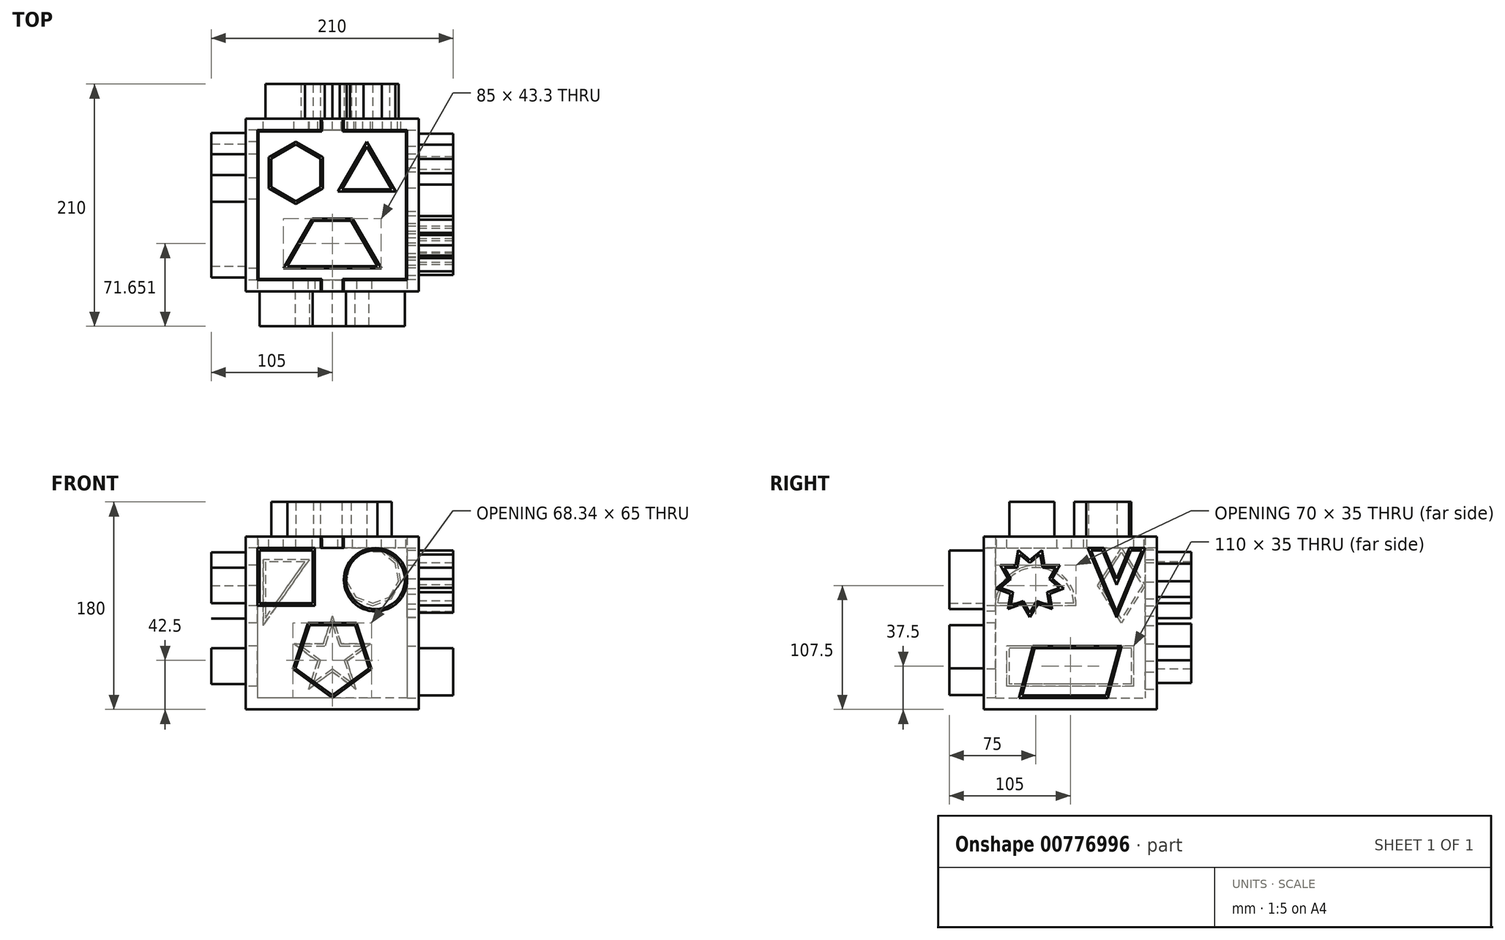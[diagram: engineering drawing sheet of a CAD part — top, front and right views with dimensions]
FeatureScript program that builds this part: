
annotation { "Feature Type Name" : "Feature", "Feature Type Description" : "" }
export const myFeature = defineFeature(function(context is Context, id is Id, definition is map)
    precondition{}
    {
        {
            var Q0;
            Q0=qCreatedBy(makeId("Top.planeOp"),FACE);
            var sketch = newSketch(context, id + "F0", { "sketchPlane" : qUnion([Q0])});
            skLineSegment(sketch, "E0.bottom", {"start": v(0, 0) * mm, "end": v(-150, 0) * mm});
            skLineSegment(sketch, "E0.top", {"start": v(0, 150) * mm, "end": v(-150, 150) * mm});
            skLineSegment(sketch, "E0.left", {"start": v(0, 0) * mm, "end": v(0, 150) * mm});
            skLineSegment(sketch, "E0.right", {"start": v(-150, 0) * mm, "end": v(-150, 150) * mm});
            skSolve(sketch);
        }
        {
            var Q0;
            Q0=makeQuery(id+"F0.imprint","IMPRINT",FACE,{"disambiguationData":[TD([[makeQuery(id+"F0.imprint","IMPRINT",EDGE,{"derivedFrom":sQuery(id+"F0.wireOp",EDGE,"E0.bottom")}),-1.0]])]});
            extrude(context, id + "F1", {"entities" : qUnion([Q0]), "depth" : 150 * mm, "offsetDistance" : 25 * mm});
        }
        {
            var Q0;
            Q0=makeQuery(id+"F1.opExtrude","CAP_FACE",FACE,{"disambiguationData":[OSD([sQuery(id+"F0.wireOp",EDGE,"E0.bottom"),sQuery(id+"F0.wireOp",EDGE,"E0.top"),sQuery(id+"F0.wireOp",EDGE,"E0.left"),sQuery(id+"F0.wireOp",EDGE,"E0.right")])],"isStart":false});
            shell(context, id + "F2", {"entities" : qUnion([Q0]), "thickness" : 10 * mm});
        }
        {
            var Q0;
            Q0=makeQuery(id+"F1.opExtrude","CAP_FACE",FACE,{"disambiguationData":[OSD([sQuery(id+"F0.wireOp",EDGE,"E0.bottom"),sQuery(id+"F0.wireOp",EDGE,"E0.top"),sQuery(id+"F0.wireOp",EDGE,"E0.left"),sQuery(id+"F0.wireOp",EDGE,"E0.right")])],"isStart":false});
            var sketch = newSketch(context, id + "F3", { "sketchPlane" : qUnion([Q0])});
            skLineSegment(sketch, "E1.bottom", {"start": v(-10, 10) * mm, "end": v(-65, 10) * mm});
            skLineSegment(sketch, "E1.top", {"start": v(-10, 140) * mm, "end": v(-65, 140) * mm});
            skLineSegment(sketch, "E1.left", {"start": v(-10, 10) * mm, "end": v(-10, 140) * mm});
            skLineSegment(sketch, "E1.right", {"start": v(-140, 10) * mm, "end": v(-140, 140) * mm});
            skPoint(sketch, "E2", {"position": v(-75, 140) * mm});
            skLineSegment(sketch, "E3", {"start": v(-75, 140) * mm, "end": v(-85, 140) * mm});
            skLineSegment(sketch, "E4", {"start": v(-85, 140) * mm, "end": v(-85, 150) * mm});
            skLineSegment(sketch, "E5", {"start": v(-85, 150) * mm, "end": v(-65, 150) * mm});
            skLineSegment(sketch, "E6", {"start": v(-65, 150) * mm, "end": v(-65, 140) * mm});
            skLineSegment(sketch, "E7", {"start": v(-65, 140) * mm, "end": v(-75, 140) * mm});
            skLineSegment(sketch, "E8", {"start": v(-140, 75) * mm, "end": v(-10, 75) * mm, "construction": true});
            skLineSegment(sketch, "E9.MirrorCS", {"start": v(-75, 10) * mm, "end": v(-85, 10) * mm});
            skLineSegment(sketch, "E10.MirrorCS", {"start": v(-65, 10) * mm, "end": v(-75, 10) * mm});
            skLineSegment(sketch, "E11.MirrorCS", {"start": v(-85, 0) * mm, "end": v(-65, 0) * mm});
            skLineSegment(sketch, "E12.MirrorCS", {"start": v(-85, 10) * mm, "end": v(-85, 0) * mm});
            skLineSegment(sketch, "E13.MirrorCS", {"start": v(-65, 0) * mm, "end": v(-65, 10) * mm});
            skLineSegment(sketch, "E14", {"start": v(-85, 140) * mm, "end": v(-140, 140) * mm});
            skLineSegment(sketch, "E15", {"start": v(-65, 140) * mm, "end": v(-85, 140) * mm});
            skLineSegment(sketch, "E16", {"start": v(-85, 10) * mm, "end": v(-140, 10) * mm});
            skLineSegment(sketch, "E17", {"start": v(-65, 10) * mm, "end": v(-85, 10) * mm});
            skLineSegment(sketch, "E18.0", {"start": v(-84, 139) * mm, "end": v(-84, 150) * mm});
            skLineSegment(sketch, "E18.1", {"start": v(-84, 11) * mm, "end": v(-84, 0) * mm});
            skLineSegment(sketch, "E18.2", {"start": v(-84, 11) * mm, "end": v(-139, 11) * mm});
            skLineSegment(sketch, "E18.3", {"start": v(-139, 11) * mm, "end": v(-139, 139) * mm});
            skLineSegment(sketch, "E18.4", {"start": v(-84, 139) * mm, "end": v(-139, 139) * mm});
            skLineSegment(sketch, "E19.0", {"start": v(5, -5) * mm, "end": v(5, 155) * mm});
            skLineSegment(sketch, "E19.1", {"start": v(-155, -5) * mm, "end": v(5, -5) * mm});
            skLineSegment(sketch, "E19.2", {"start": v(-155, 155) * mm, "end": v(-155, -5) * mm});
            skLineSegment(sketch, "E19.3", {"start": v(5, 155) * mm, "end": v(-155, 155) * mm});
            skLineSegment(sketch, "E20.0", {"start": v(-66, 0) * mm, "end": v(-66, 11) * mm});
            skLineSegment(sketch, "E20.1", {"start": v(-66, 150) * mm, "end": v(-66, 139) * mm});
            skLineSegment(sketch, "E20.2", {"start": v(-11, 139) * mm, "end": v(-66, 139) * mm});
            skLineSegment(sketch, "E20.3", {"start": v(-11, 11) * mm, "end": v(-11, 139) * mm});
            skLineSegment(sketch, "E20.4", {"start": v(-11, 11) * mm, "end": v(-66, 11) * mm});
            skSolve(sketch);
        }
        {
            var Q0;
            {var subQ3=sQuery(id+"F3.wireOp",EDGE,"E1.left");Q0=makeQuery(id+"F3.imprint","IMPRINT",FACE,{"disambiguationData":[TD([[makeQuery(id+"F3.imprint","IMPRINT",EDGE,{"derivedFrom":subQ3}),1.0]])]});}
            var sketch = newSketch(context, id + "F4", { "sketchPlane" : qUnion([Q0])});
            skCircle(sketch, "E21.cCircle", {"center": v(-106.62, 103) * mm, "radius": 23.38 * mm, "construction": true});
            skLineSegment(sketch, "E21.0", {"start": v(-106.62, 130) * mm, "end": v(-83.23, 116.5) * mm});
            skLineSegment(sketch, "E21.1", {"start": v(-83.23, 116.5) * mm, "end": v(-83.23, 89.5) * mm});
            skLineSegment(sketch, "E21.2", {"start": v(-83.23, 89.5) * mm, "end": v(-106.62, 76) * mm});
            skLineSegment(sketch, "E21.3", {"start": v(-106.62, 76) * mm, "end": v(-130, 89.5) * mm});
            skLineSegment(sketch, "E21.4", {"start": v(-130, 89.5) * mm, "end": v(-130, 116.5) * mm});
            skLineSegment(sketch, "E21.5", {"start": v(-130, 116.5) * mm, "end": v(-106.62, 130) * mm});
            skPoint(sketch, "E21.0.midPoint", {"position": v(-94.93, 123.25) * mm});
            skCircle(sketch, "E22.cCircle", {"center": v(-45, 101.13) * mm, "radius": 14.43 * mm, "construction": true});
            skLineSegment(sketch, "E22.0", {"start": v(-45, 130) * mm, "end": v(-20, 86.7) * mm});
            skLineSegment(sketch, "E22.1", {"start": v(-20, 86.7) * mm, "end": v(-70, 86.7) * mm});
            skLineSegment(sketch, "E22.2", {"start": v(-70, 86.7) * mm, "end": v(-45, 130) * mm});
            skPoint(sketch, "E22.0.midPoint", {"position": v(-32.5, 108.35) * mm});
            skLineSegment(sketch, "E23", {"start": v(-117.5, 20) * mm, "end": v(-92.5, 63.3) * mm});
            skLineSegment(sketch, "E24", {"start": v(-92.5, 63.3) * mm, "end": v(-57.5, 63.3) * mm});
            skLineSegment(sketch, "E25", {"start": v(-57.5, 63.3) * mm, "end": v(-32.5, 20) * mm});
            skLineSegment(sketch, "E26", {"start": v(-32.5, 20) * mm, "end": v(-117.5, 20) * mm});
            skPoint(sketch, "E27", {"position": v(-75, 20) * mm});
            skPoint(sketch, "E28.0", {"position": v(-75, 10) * mm});
            skLineSegment(sketch, "E29", {"start": v(-75, 20) * mm, "end": v(-75, 10) * mm, "construction": true});
            skLineSegment(sketch, "E30.0", {"start": v(-128, 90.65) * mm, "end": v(-128, 115.35) * mm});
            skLineSegment(sketch, "E30.1", {"start": v(-106.62, 127.7) * mm, "end": v(-85.23, 115.35) * mm});
            skLineSegment(sketch, "E30.2", {"start": v(-85.23, 115.35) * mm, "end": v(-85.23, 90.65) * mm});
            skLineSegment(sketch, "E30.3", {"start": v(-128, 115.35) * mm, "end": v(-106.62, 127.7) * mm});
            skLineSegment(sketch, "E30.4", {"start": v(-85.23, 90.65) * mm, "end": v(-106.62, 78.3) * mm});
            skLineSegment(sketch, "E30.5", {"start": v(-106.62, 78.3) * mm, "end": v(-128, 90.65) * mm});
            skLineSegment(sketch, "E31.0", {"start": v(-16, 134) * mm, "end": v(-71, 134) * mm});
            skLineSegment(sketch, "E31.1", {"start": v(-134, 134) * mm, "end": v(-134, 16) * mm});
            skLineSegment(sketch, "E31.2", {"start": v(-79, 134) * mm, "end": v(-134, 134) * mm});
            skLineSegment(sketch, "E31.3", {"start": v(-79, 135) * mm, "end": v(-79, 134) * mm});
            skLineSegment(sketch, "E31.4", {"start": v(-71, 135) * mm, "end": v(-79, 135) * mm});
            skLineSegment(sketch, "E31.5", {"start": v(-134, 16) * mm, "end": v(-79, 16) * mm});
            skLineSegment(sketch, "E31.6", {"start": v(-71, 134) * mm, "end": v(-71, 135) * mm});
            skLineSegment(sketch, "E31.7", {"start": v(-79, 16) * mm, "end": v(-79, 15) * mm});
            skLineSegment(sketch, "E31.8", {"start": v(-79, 15) * mm, "end": v(-71, 15) * mm});
            skLineSegment(sketch, "E31.9", {"start": v(-71, 15) * mm, "end": v(-71, 16) * mm});
            skLineSegment(sketch, "E31.10", {"start": v(-71, 16) * mm, "end": v(-16, 16) * mm});
            skLineSegment(sketch, "E31.11", {"start": v(-16, 16) * mm, "end": v(-16, 134) * mm});
            skLineSegment(sketch, "E32.0", {"start": v(-66.54, 88.7) * mm, "end": v(-45, 126) * mm});
            skLineSegment(sketch, "E32.1", {"start": v(-23.46, 88.7) * mm, "end": v(-66.54, 88.7) * mm});
            skLineSegment(sketch, "E32.2", {"start": v(-45, 126) * mm, "end": v(-23.46, 88.7) * mm});
            skLineSegment(sketch, "E33.0", {"start": v(-91.35, 61.3) * mm, "end": v(-58.65, 61.3) * mm});
            skLineSegment(sketch, "E33.1", {"start": v(-114.04, 22) * mm, "end": v(-91.35, 61.3) * mm});
            skLineSegment(sketch, "E33.2", {"start": v(-35.96, 22) * mm, "end": v(-114.04, 22) * mm});
            skLineSegment(sketch, "E33.3", {"start": v(-58.65, 61.3) * mm, "end": v(-35.96, 22) * mm});
            skSolve(sketch);
        }
        {
            var Q0;
            {var subQ0=sQuery(id+"F3.wireOp",EDGE,"E6");Q0=makeQuery(id+"F3.imprint","IMPRINT",FACE,{"disambiguationData":[TD([[makeQuery(id+"F3.imprint","IMPRINT",EDGE,{"derivedFrom":subQ0}),-1.0]])]});}
            var Q1;
            {var subQ0=sQuery(id+"F3.wireOp",EDGE,"E18.0");var subQ1=sQuery(id+"F3.wireOp",EDGE,"E5");var subQ2=makeQuery(id+"F3.imprint","INTERSECT",VERTEX,{"derivedFrom":[subQ1,subQ0]});Q1=makeQuery(id+"F3.imprint","IMPRINT",FACE,{"disambiguationData":[TD([[makeQuery(id+"F3.imprint","IMPRINT",EDGE,{"disambiguationData":[TD([[subQ2,1.0]])],"derivedFrom":subQ1}),1.0]])]});}
            var Q2;
            {var subQ0=sQuery(id+"F3.wireOp",EDGE,"E4");Q2=makeQuery(id+"F3.imprint","IMPRINT",FACE,{"disambiguationData":[TD([[makeQuery(id+"F3.imprint","IMPRINT",EDGE,{"derivedFrom":subQ0}),-1.0]])]});}
            var Q3;
            Q3=makeQuery(id+"F3.imprint","IMPRINT",FACE,{"disambiguationData":[TD([[makeQuery(id+"F3.imprint","IMPRINT",EDGE,{"derivedFrom":sQuery(id+"F3.wireOp",EDGE,"E1.right")}),-1.0]])]});
            var Q4;
            {var subQ9=sQuery(id+"F3.wireOp",EDGE,"E18.2");Q4=makeQuery(id+"F3.imprint","IMPRINT",FACE,{"disambiguationData":[TD([[makeQuery(id+"F3.imprint","IMPRINT",EDGE,{"derivedFrom":subQ9}),-1.0]])]});}
            var Q5;
            {var subQ5=sQuery(id+"F3.wireOp",EDGE,"E1.bottom");Q5=makeQuery(id+"F3.imprint","IMPRINT",FACE,{"disambiguationData":[TD([[makeQuery(id+"F3.imprint","IMPRINT",EDGE,{"derivedFrom":subQ5}),-1.0]])]});}
            var Q6;
            {var subQ0=sQuery(id+"F3.wireOp",EDGE,"E12.MirrorCS");Q6=makeQuery(id+"F3.imprint","IMPRINT",FACE,{"disambiguationData":[TD([[makeQuery(id+"F3.imprint","IMPRINT",EDGE,{"derivedFrom":subQ0}),1.0]])]});}
            var Q7;
            {var subQ0=sQuery(id+"F3.wireOp",EDGE,"E18.1");var subQ1=sQuery(id+"F3.wireOp",EDGE,"E11.MirrorCS");var subQ2=makeQuery(id+"F3.imprint","INTERSECT",VERTEX,{"derivedFrom":[subQ1,subQ0]});Q7=makeQuery(id+"F3.imprint","IMPRINT",FACE,{"disambiguationData":[TD([[makeQuery(id+"F3.imprint","IMPRINT",EDGE,{"disambiguationData":[TD([[subQ2,1.0]])],"derivedFrom":subQ1}),-1.0]])]});}
            var Q8;
            {var subQ0=sQuery(id+"F3.wireOp",EDGE,"E13.MirrorCS");Q8=makeQuery(id+"F3.imprint","IMPRINT",FACE,{"disambiguationData":[TD([[makeQuery(id+"F3.imprint","IMPRINT",EDGE,{"derivedFrom":subQ0}),1.0]])]});}
            extrude(context, id + "F5", {"entities" : qUnion([Q0, Q1, Q2, Q3, Q4, Q5, Q6, Q7, Q8]), "operationType" : NewBodyOperationType.REMOVE, "oppositeDirection" : true, "depth" : 10 * mm, "offsetDistance" : 25 * mm});
        }
        {
            var Q0;
            {var subQ0=sQuery(id+"F3.wireOp",EDGE,"E18.0");var subQ1=sQuery(id+"F3.wireOp",EDGE,"E5");var subQ2=makeQuery(id+"F3.imprint","INTERSECT",VERTEX,{"derivedFrom":[subQ1,subQ0]});Q0=makeQuery(id+"F3.imprint","IMPRINT",FACE,{"disambiguationData":[TD([[makeQuery(id+"F3.imprint","IMPRINT",EDGE,{"disambiguationData":[TD([[subQ2,1.0]])],"derivedFrom":subQ1}),1.0]])]});}
            var Q1;
            {var subQ9=sQuery(id+"F3.wireOp",EDGE,"E18.2");Q1=makeQuery(id+"F3.imprint","IMPRINT",FACE,{"disambiguationData":[TD([[makeQuery(id+"F3.imprint","IMPRINT",EDGE,{"derivedFrom":subQ9}),-1.0]])]});}
            var Q2;
            {var subQ0=sQuery(id+"F3.wireOp",EDGE,"E18.1");var subQ1=sQuery(id+"F3.wireOp",EDGE,"E11.MirrorCS");var subQ2=makeQuery(id+"F3.imprint","INTERSECT",VERTEX,{"derivedFrom":[subQ1,subQ0]});Q2=makeQuery(id+"F3.imprint","IMPRINT",FACE,{"disambiguationData":[TD([[makeQuery(id+"F3.imprint","IMPRINT",EDGE,{"disambiguationData":[TD([[subQ2,1.0]])],"derivedFrom":subQ1}),-1.0]])]});}
            extrude(context, id + "F6", {"entities" : qUnion([Q0, Q1, Q2]), "depth" : -10 * mm, "offsetDistance" : 25 * mm});
        }
        {
            var Q0;
            Q0=makeQuery(id+"F4.imprint","IMPRINT",FACE,{"disambiguationData":[TD([[makeQuery(id+"F4.imprint","IMPRINT",EDGE,{"derivedFrom":sQuery(id+"F4.wireOp",EDGE,"E23")}),-1.0]])]});
            var Q1;
            Q1=makeQuery(id+"F4.imprint","IMPRINT",FACE,{"disambiguationData":[TD([[makeQuery(id+"F4.imprint","IMPRINT",EDGE,{"derivedFrom":sQuery(id+"F4.wireOp",EDGE,"E33.0")}),-1.0]])]});
            var Q2;
            Q2=makeQuery(id+"F4.imprint","IMPRINT",FACE,{"disambiguationData":[TD([[makeQuery(id+"F4.imprint","IMPRINT",EDGE,{"derivedFrom":sQuery(id+"F4.wireOp",EDGE,"E21.0")}),-1.0]])]});
            var Q3;
            Q3=makeQuery(id+"F4.imprint","IMPRINT",FACE,{"disambiguationData":[TD([[makeQuery(id+"F4.imprint","IMPRINT",EDGE,{"derivedFrom":sQuery(id+"F4.wireOp",EDGE,"E30.0")}),-1.0]])]});
            var Q4;
            Q4=makeQuery(id+"F4.imprint","IMPRINT",FACE,{"disambiguationData":[TD([[makeQuery(id+"F4.imprint","IMPRINT",EDGE,{"derivedFrom":sQuery(id+"F4.wireOp",EDGE,"E32.0")}),-1.0]])]});
            var Q5;
            Q5=makeQuery(id+"F4.imprint","IMPRINT",FACE,{"disambiguationData":[TD([[makeQuery(id+"F4.imprint","IMPRINT",EDGE,{"derivedFrom":sQuery(id+"F4.wireOp",EDGE,"E22.0")}),-1.0]])]});
            extrude(context, id + "F7", {"entities" : qUnion([Q0, Q1, Q2, Q3, Q4, Q5]), "operationType" : NewBodyOperationType.REMOVE, "oppositeDirection" : true, "depth" : 25 * mm, "offsetDistance" : 25 * mm});
        }
        {
            var Q0;
            Q0=makeQuery(id+"F4.imprint","IMPRINT",FACE,{"disambiguationData":[TD([[makeQuery(id+"F4.imprint","IMPRINT",EDGE,{"derivedFrom":sQuery(id+"F4.wireOp",EDGE,"E33.0")}),-1.0]])]});
            var Q1;
            Q1=makeQuery(id+"F4.imprint","IMPRINT",FACE,{"disambiguationData":[TD([[makeQuery(id+"F4.imprint","IMPRINT",EDGE,{"derivedFrom":sQuery(id+"F4.wireOp",EDGE,"E32.0")}),-1.0]])]});
            var Q2;
            Q2=makeQuery(id+"F4.imprint","IMPRINT",FACE,{"disambiguationData":[TD([[makeQuery(id+"F4.imprint","IMPRINT",EDGE,{"derivedFrom":sQuery(id+"F4.wireOp",EDGE,"E30.0")}),-1.0]])]});
            extrude(context, id + "F8", {"entities" : qUnion([Q0, Q1, Q2]), "depth" : 30 * mm, "offsetDistance" : 25 * mm});
        }
        {
            var Q0;
            Q0=makeQuery(id+"F1.opExtrude","SWEPT_FACE",FACE,{"disambiguationData":[OSD([sQuery(id+"F0.wireOp",EDGE,"E0.bottom")])]});
            var sketch = newSketch(context, id + "F9", { "sketchPlane" : qUnion([Q0])});
            skLineSegment(sketch, "E34.bottom", {"start": v(-140, 140) * mm, "end": v(-90, 140) * mm});
            skLineSegment(sketch, "E34.top", {"start": v(-140, 90) * mm, "end": v(-90, 90) * mm});
            skLineSegment(sketch, "E34.left", {"start": v(-140, 140) * mm, "end": v(-140, 90) * mm});
            skLineSegment(sketch, "E34.right", {"start": v(-90, 140) * mm, "end": v(-90, 90) * mm});
            skCircle(sketch, "E35", {"center": v(-37.5, 112.5) * mm, "radius": 27.5 * mm});
            skPoint(sketch, "E35.centerSnap0", {"position": v(-90, 115) * mm});
            skCircle(sketch, "E36.cCircle", {"center": v(-75, 45.93) * mm, "radius": 29.07 * mm, "construction": true});
            skPoint(sketch, "E36.cCircle.centerSnap0", {"position": v(-75, 0) * mm});
            skLineSegment(sketch, "E36.0", {"start": v(-53.88, 75) * mm, "end": v(-40.83, 34.83) * mm});
            skLineSegment(sketch, "E36.1", {"start": v(-40.83, 34.83) * mm, "end": v(-75, 10) * mm});
            skLineSegment(sketch, "E36.2", {"start": v(-75, 10) * mm, "end": v(-109.17, 34.83) * mm});
            skLineSegment(sketch, "E36.3", {"start": v(-109.17, 34.83) * mm, "end": v(-96.12, 75) * mm});
            skLineSegment(sketch, "E36.4", {"start": v(-96.12, 75) * mm, "end": v(-53.88, 75) * mm});
            skPoint(sketch, "E36.0.midPoint", {"position": v(-47.35, 54.91) * mm});
            skLineSegment(sketch, "E37.0", {"start": v(-138, 138) * mm, "end": v(-92, 138) * mm});
            skLineSegment(sketch, "E37.1", {"start": v(-138, 138) * mm, "end": v(-138, 92) * mm});
            skLineSegment(sketch, "E37.2", {"start": v(-138, 92) * mm, "end": v(-92, 92) * mm});
            skLineSegment(sketch, "E37.3", {"start": v(-92, 138) * mm, "end": v(-92, 92) * mm});
            skLineSegment(sketch, "E38.0", {"start": v(-70, 155) * mm, "end": v(-70, 145) * mm});
            skLineSegment(sketch, "E38.1", {"start": v(5, 155) * mm, "end": v(-70, 155) * mm});
            skLineSegment(sketch, "E38.2", {"start": v(-70, 145) * mm, "end": v(-80, 145) * mm});
            skLineSegment(sketch, "E38.3", {"start": v(5, -5) * mm, "end": v(5, 155) * mm});
            skLineSegment(sketch, "E38.4", {"start": v(-80, 145) * mm, "end": v(-80, 155) * mm});
            skLineSegment(sketch, "E38.5", {"start": v(-80, 155) * mm, "end": v(-155, 155) * mm});
            skLineSegment(sketch, "E38.6", {"start": v(-155, 155) * mm, "end": v(-155, -5) * mm});
            skLineSegment(sketch, "E38.7", {"start": v(-155, -5) * mm, "end": v(5, -5) * mm});
            skCircle(sketch, "E39.0", {"center": v(-37.5, 112.5) * mm, "radius": 25.5 * mm});
            skLineSegment(sketch, "E40.0", {"start": v(-55.33, 73) * mm, "end": v(-43.18, 35.6) * mm});
            skLineSegment(sketch, "E40.1", {"start": v(-94.67, 73) * mm, "end": v(-55.33, 73) * mm});
            skLineSegment(sketch, "E40.2", {"start": v(-43.18, 35.6) * mm, "end": v(-75, 12.47) * mm});
            skLineSegment(sketch, "E40.3", {"start": v(-75, 12.47) * mm, "end": v(-106.82, 35.6) * mm});
            skLineSegment(sketch, "E40.4", {"start": v(-106.82, 35.6) * mm, "end": v(-94.67, 73) * mm});
            skSolve(sketch);
        }
        {
            var Q0;
            Q0=makeQuery(id+"F9.imprint","IMPRINT",FACE,{"disambiguationData":[TD([[makeQuery(id+"F9.imprint","IMPRINT",EDGE,{"derivedFrom":sQuery(id+"F9.wireOp",EDGE,"E34.bottom")}),-1.0]])]});
            var Q1;
            Q1=makeQuery(id+"F9.imprint","IMPRINT",FACE,{"disambiguationData":[TD([[makeQuery(id+"F9.imprint","IMPRINT",EDGE,{"derivedFrom":sQuery(id+"F9.wireOp",EDGE,"E37.0")}),-1.0]])]});
            var Q2;
            Q2=makeQuery(id+"F9.imprint","IMPRINT",FACE,{"disambiguationData":[TD([[makeQuery(id+"F9.imprint","IMPRINT",EDGE,{"derivedFrom":sQuery(id+"F9.wireOp",EDGE,"E35")}),1.0]])]});
            var Q3;
            Q3=makeQuery(id+"F9.imprint","IMPRINT",FACE,{"disambiguationData":[TD([[makeQuery(id+"F9.imprint","IMPRINT",EDGE,{"derivedFrom":sQuery(id+"F9.wireOp",EDGE,"E39.0")}),1.0]])]});
            var Q4;
            Q4=makeQuery(id+"F9.imprint","IMPRINT",FACE,{"disambiguationData":[TD([[makeQuery(id+"F9.imprint","IMPRINT",EDGE,{"derivedFrom":sQuery(id+"F9.wireOp",EDGE,"E36.0")}),-1.0]])]});
            var Q5;
            Q5=makeQuery(id+"F9.imprint","IMPRINT",FACE,{"disambiguationData":[TD([[makeQuery(id+"F9.imprint","IMPRINT",EDGE,{"derivedFrom":sQuery(id+"F9.wireOp",EDGE,"E40.0")}),-1.0]])]});
            extrude(context, id + "F10", {"entities" : qUnion([Q0, Q1, Q2, Q3, Q4, Q5]), "operationType" : NewBodyOperationType.REMOVE, "oppositeDirection" : true, "depth" : 25 * mm, "offsetDistance" : 25 * mm});
        }
        {
            var Q0;
            Q0=makeQuery(id+"F9.imprint","IMPRINT",FACE,{"disambiguationData":[TD([[makeQuery(id+"F9.imprint","IMPRINT",EDGE,{"derivedFrom":sQuery(id+"F9.wireOp",EDGE,"E37.0")}),-1.0]])]});
            var Q1;
            Q1=makeQuery(id+"F9.imprint","IMPRINT",FACE,{"disambiguationData":[TD([[makeQuery(id+"F9.imprint","IMPRINT",EDGE,{"derivedFrom":sQuery(id+"F9.wireOp",EDGE,"E39.0")}),1.0]])]});
            var Q2;
            Q2=makeQuery(id+"F9.imprint","IMPRINT",FACE,{"disambiguationData":[TD([[makeQuery(id+"F9.imprint","IMPRINT",EDGE,{"derivedFrom":sQuery(id+"F9.wireOp",EDGE,"E40.0")}),-1.0]])]});
            extrude(context, id + "F11", {"entities" : qUnion([Q0, Q1, Q2]), "depth" : 30 * mm, "offsetDistance" : 25 * mm});
        }
        {
            var Q0;
            Q0=makeQuery(id+"F1.opExtrude","SWEPT_FACE",FACE,{"disambiguationData":[OSD([sQuery(id+"F0.wireOp",EDGE,"E0.right")])]});
            var sketch = newSketch(context, id + "F12", { "sketchPlane" : qUnion([Q0])});
            skLineSegment(sketch, "E41", {"start": v(-119.3, 140) * mm, "end": v(-140, 107.5) * mm});
            skLineSegment(sketch, "E42", {"start": v(-140, 107.5) * mm, "end": v(-119.3, 75) * mm});
            skLineSegment(sketch, "E43", {"start": v(-119.3, 75) * mm, "end": v(-98.6, 107.5) * mm});
            skLineSegment(sketch, "E44", {"start": v(-98.6, 107.5) * mm, "end": v(-119.3, 140) * mm});
            skLineSegment(sketch, "E45", {"start": v(-119.3, 75) * mm, "end": v(-119.3, 140) * mm, "construction": true});
            skLineSegment(sketch, "E46", {"start": v(-140, 107.5) * mm, "end": v(-98.6, 107.5) * mm, "construction": true});
            skArc(sketch, "E47", {"start": v(-10, 90) * mm, "mid": v(-45, 125) * mm, "end": v(-80, 90) * mm});
            skLineSegment(sketch, "E48", {"start": v(-80, 90) * mm, "end": v(-10, 90) * mm});
            skLineSegment(sketch, "E49.bottom", {"start": v(-130, 20) * mm, "end": v(-20, 20) * mm});
            skLineSegment(sketch, "E49.top", {"start": v(-130, 55) * mm, "end": v(-20, 55) * mm});
            skLineSegment(sketch, "E49.left", {"start": v(-130, 20) * mm, "end": v(-130, 55) * mm});
            skLineSegment(sketch, "E49.right", {"start": v(-20, 20) * mm, "end": v(-20, 55) * mm});
            skLineSegment(sketch, "E50.0", {"start": v(-119.3, 136.28) * mm, "end": v(-137.63, 107.5) * mm});
            skLineSegment(sketch, "E50.1", {"start": v(-100.96, 107.5) * mm, "end": v(-119.3, 136.28) * mm});
            skLineSegment(sketch, "E50.2", {"start": v(-119.3, 78.72) * mm, "end": v(-100.96, 107.5) * mm});
            skLineSegment(sketch, "E50.3", {"start": v(-137.63, 107.5) * mm, "end": v(-119.3, 78.72) * mm});
            skLineSegment(sketch, "E51.0", {"start": v(-145, 5) * mm, "end": v(-5, 5) * mm});
            skLineSegment(sketch, "E51.1", {"start": v(-145, 145) * mm, "end": v(-145, 5) * mm});
            skLineSegment(sketch, "E51.2", {"start": v(-5, 145) * mm, "end": v(-145, 145) * mm});
            skLineSegment(sketch, "E51.3", {"start": v(-5, 5) * mm, "end": v(-5, 145) * mm});
            skArc(sketch, "E52.0", {"start": v(-12.06, 92) * mm, "mid": v(-45, 123) * mm, "end": v(-77.94, 92) * mm});
            skLineSegment(sketch, "E52.1", {"start": v(-77.94, 92) * mm, "end": v(-12.06, 92) * mm});
            skLineSegment(sketch, "E53.0", {"start": v(-128, 53) * mm, "end": v(-22, 53) * mm});
            skLineSegment(sketch, "E53.1", {"start": v(-128, 22) * mm, "end": v(-128, 53) * mm});
            skLineSegment(sketch, "E53.2", {"start": v(-128, 22) * mm, "end": v(-22, 22) * mm});
            skLineSegment(sketch, "E53.3", {"start": v(-22, 22) * mm, "end": v(-22, 53) * mm});
            skSolve(sketch);
        }
        {
            var Q0;
            Q0=makeQuery(id+"F12.imprint","IMPRINT",FACE,{"disambiguationData":[TD([[makeQuery(id+"F12.imprint","IMPRINT",EDGE,{"derivedFrom":sQuery(id+"F12.wireOp",EDGE,"E50.0")}),1.0]])]});
            var Q1;
            Q1=makeQuery(id+"F12.imprint","IMPRINT",FACE,{"disambiguationData":[TD([[makeQuery(id+"F12.imprint","IMPRINT",EDGE,{"derivedFrom":sQuery(id+"F12.wireOp",EDGE,"E41")}),1.0]])]});
            var Q2;
            Q2=makeQuery(id+"F12.imprint","IMPRINT",FACE,{"disambiguationData":[TD([[makeQuery(id+"F12.imprint","IMPRINT",EDGE,{"derivedFrom":sQuery(id+"F12.wireOp",EDGE,"E52.0")}),1.0]])]});
            var Q3;
            Q3=makeQuery(id+"F12.imprint","IMPRINT",FACE,{"disambiguationData":[TD([[makeQuery(id+"F12.imprint","IMPRINT",EDGE,{"derivedFrom":sQuery(id+"F12.wireOp",EDGE,"E47")}),1.0]])]});
            var Q4;
            Q4=makeQuery(id+"F12.imprint","IMPRINT",FACE,{"disambiguationData":[TD([[makeQuery(id+"F12.imprint","IMPRINT",EDGE,{"derivedFrom":sQuery(id+"F12.wireOp",EDGE,"E53.0")}),-1.0]])]});
            var Q5;
            Q5=makeQuery(id+"F12.imprint","IMPRINT",FACE,{"disambiguationData":[TD([[makeQuery(id+"F12.imprint","IMPRINT",EDGE,{"derivedFrom":sQuery(id+"F12.wireOp",EDGE,"E49.bottom")}),1.0]])]});
            extrude(context, id + "F13", {"entities" : qUnion([Q0, Q1, Q2, Q3, Q4, Q5]), "operationType" : NewBodyOperationType.REMOVE, "oppositeDirection" : true, "depth" : 25 * mm, "offsetDistance" : 25 * mm});
        }
        {
            var Q0;
            Q0=makeQuery(id+"F12.imprint","IMPRINT",FACE,{"disambiguationData":[TD([[makeQuery(id+"F12.imprint","IMPRINT",EDGE,{"derivedFrom":sQuery(id+"F12.wireOp",EDGE,"E50.0")}),1.0]])]});
            var Q1;
            Q1=makeQuery(id+"F12.imprint","IMPRINT",FACE,{"disambiguationData":[TD([[makeQuery(id+"F12.imprint","IMPRINT",EDGE,{"derivedFrom":sQuery(id+"F12.wireOp",EDGE,"E52.0")}),1.0]])]});
            var Q2;
            Q2=makeQuery(id+"F12.imprint","IMPRINT",FACE,{"disambiguationData":[TD([[makeQuery(id+"F12.imprint","IMPRINT",EDGE,{"derivedFrom":sQuery(id+"F12.wireOp",EDGE,"E53.0")}),-1.0]])]});
            extrude(context, id + "F14", {"entities" : qUnion([Q0, Q1, Q2]), "depth" : 30 * mm, "offsetDistance" : 25 * mm});
        }
        {
            var Q0;
            Q0=makeQuery(id+"F1.opExtrude","SWEPT_FACE",FACE,{"disambiguationData":[OSD([sQuery(id+"F0.wireOp",EDGE,"E0.top")])]});
            var sketch = newSketch(context, id + "F15", { "sketchPlane" : qUnion([Q0])});
            skCircle(sketch, "E54.cCircle", {"center": v(75, 45.93) * mm, "radius": 35 * mm, "construction": true});
            skLineSegment(sketch, "E54.0", {"start": v(108.29, 56.75) * mm, "end": v(95.57, 17.62) * mm, "construction": true});
            skLineSegment(sketch, "E54.1", {"start": v(95.57, 17.62) * mm, "end": v(54.43, 17.62) * mm, "construction": true});
            skLineSegment(sketch, "E54.2", {"start": v(54.43, 17.62) * mm, "end": v(41.71, 56.75) * mm, "construction": true});
            skLineSegment(sketch, "E54.3", {"start": v(41.71, 56.75) * mm, "end": v(75, 80.93) * mm, "construction": true});
            skLineSegment(sketch, "E54.4", {"start": v(75, 80.93) * mm, "end": v(108.29, 56.75) * mm, "construction": true});
            skLineSegment(sketch, "E55", {"start": v(75, 80.93) * mm, "end": v(82.86, 56.75) * mm, "construction": true});
            skLineSegment(sketch, "E56", {"start": v(41.71, 56.75) * mm, "end": v(62.29, 41.8) * mm, "construction": true});
            skLineSegment(sketch, "E57", {"start": v(54.43, 17.62) * mm, "end": v(75, 32.56) * mm, "construction": true});
            skLineSegment(sketch, "E58", {"start": v(75, 80.93) * mm, "end": v(67.14, 56.75) * mm, "construction": true});
            skLineSegment(sketch, "E59", {"start": v(41.71, 56.75) * mm, "end": v(67.14, 56.75) * mm, "construction": true});
            skLineSegment(sketch, "E60", {"start": v(75, 80.93) * mm, "end": v(82.86, 56.75) * mm});
            skLineSegment(sketch, "E61", {"start": v(82.86, 56.75) * mm, "end": v(108.29, 56.75) * mm});
            skLineSegment(sketch, "E62", {"start": v(108.29, 56.75) * mm, "end": v(87.71, 41.8) * mm});
            skLineSegment(sketch, "E63", {"start": v(87.71, 41.8) * mm, "end": v(95.57, 17.62) * mm});
            skLineSegment(sketch, "E64", {"start": v(95.57, 17.62) * mm, "end": v(75, 32.56) * mm});
            skLineSegment(sketch, "E65", {"start": v(75, 32.56) * mm, "end": v(54.43, 17.62) * mm});
            skLineSegment(sketch, "E66", {"start": v(54.43, 17.62) * mm, "end": v(62.29, 41.8) * mm});
            skLineSegment(sketch, "E67", {"start": v(62.29, 41.8) * mm, "end": v(41.71, 56.75) * mm});
            skLineSegment(sketch, "E68", {"start": v(41.71, 56.75) * mm, "end": v(67.14, 56.75) * mm});
            skLineSegment(sketch, "E69", {"start": v(67.14, 56.75) * mm, "end": v(75, 80.93) * mm});
            skLineSegment(sketch, "E70.trimOffspring", {"start": v(62.29, 41.8) * mm, "end": v(54.43, 17.62) * mm, "construction": true});
            skLineSegment(sketch, "E71.trimOffspring", {"start": v(82.86, 56.75) * mm, "end": v(108.29, 56.75) * mm, "construction": true});
            skLineSegment(sketch, "E72.trimOffspring", {"start": v(87.71, 41.8) * mm, "end": v(95.57, 17.62) * mm, "construction": true});
            skLineSegment(sketch, "E73.trimOffspring", {"start": v(87.71, 41.8) * mm, "end": v(108.29, 56.75) * mm, "construction": true});
            skLineSegment(sketch, "E74.trimOffspring", {"start": v(75, 32.56) * mm, "end": v(95.57, 17.62) * mm, "construction": true});
            skLineSegment(sketch, "E75.0", {"start": v(75, 74.46) * mm, "end": v(81.4, 54.75) * mm});
            skLineSegment(sketch, "E75.1", {"start": v(81.4, 54.75) * mm, "end": v(102.13, 54.75) * mm});
            skLineSegment(sketch, "E75.2", {"start": v(75, 74.46) * mm, "end": v(68.6, 54.75) * mm});
            skLineSegment(sketch, "E75.3", {"start": v(85.36, 42.56) * mm, "end": v(102.13, 54.75) * mm});
            skLineSegment(sketch, "E75.4", {"start": v(85.36, 42.56) * mm, "end": v(91.77, 22.85) * mm});
            skLineSegment(sketch, "E75.5", {"start": v(75, 35.03) * mm, "end": v(91.77, 22.85) * mm});
            skLineSegment(sketch, "E75.6", {"start": v(47.87, 54.75) * mm, "end": v(68.6, 54.75) * mm});
            skLineSegment(sketch, "E75.7", {"start": v(47.87, 54.75) * mm, "end": v(64.64, 42.56) * mm});
            skLineSegment(sketch, "E75.8", {"start": v(64.64, 42.56) * mm, "end": v(58.23, 22.85) * mm});
            skLineSegment(sketch, "E75.9", {"start": v(58.23, 22.85) * mm, "end": v(75, 35.03) * mm});
            skLineSegment(sketch, "E76.0", {"start": v(90, 145) * mm, "end": v(90, 135) * mm});
            skLineSegment(sketch, "E76.1", {"start": v(145, 145) * mm, "end": v(90, 145) * mm});
            skLineSegment(sketch, "E76.2", {"start": v(90, 135) * mm, "end": v(60, 135) * mm});
            skLineSegment(sketch, "E76.3", {"start": v(145, 5) * mm, "end": v(145, 145) * mm});
            skLineSegment(sketch, "E76.4", {"start": v(60, 135) * mm, "end": v(60, 145) * mm});
            skLineSegment(sketch, "E76.5", {"start": v(60, 145) * mm, "end": v(5, 145) * mm});
            skLineSegment(sketch, "E76.6", {"start": v(5, 145) * mm, "end": v(5, 5) * mm});
            skLineSegment(sketch, "E76.7", {"start": v(5, 5) * mm, "end": v(145, 5) * mm});
            skLineSegment(sketch, "E77", {"start": v(95, 130) * mm, "end": v(135, 130) * mm});
            skLineSegment(sketch, "E78", {"start": v(135, 130) * mm, "end": v(135, 72.87) * mm});
            skLineSegment(sketch, "E79", {"start": v(135, 72.87) * mm, "end": v(95, 130) * mm});
            skCircle(sketch, "E80.cCircle", {"center": v(40, 115) * mm, "radius": 25 * mm, "construction": true});
            skLineSegment(sketch, "E80.0", {"start": v(61.65, 127.5) * mm, "end": v(64.62, 110.66) * mm, "construction": true});
            skLineSegment(sketch, "E80.1", {"start": v(64.62, 110.66) * mm, "end": v(56.07, 95.85) * mm, "construction": true});
            skLineSegment(sketch, "E80.2", {"start": v(56.07, 95.85) * mm, "end": v(40, 90) * mm, "construction": true});
            skLineSegment(sketch, "E80.3", {"start": v(40, 90) * mm, "end": v(23.93, 95.85) * mm, "construction": true});
            skLineSegment(sketch, "E80.4", {"start": v(23.93, 95.85) * mm, "end": v(15.38, 110.66) * mm, "construction": true});
            skLineSegment(sketch, "E80.5", {"start": v(15.38, 110.66) * mm, "end": v(18.35, 127.5) * mm, "construction": true});
            skLineSegment(sketch, "E80.6", {"start": v(18.35, 127.5) * mm, "end": v(31.45, 138.5) * mm, "construction": true});
            skLineSegment(sketch, "E80.7", {"start": v(31.45, 138.5) * mm, "end": v(48.55, 138.5) * mm, "construction": true});
            skLineSegment(sketch, "E80.8", {"start": v(48.55, 138.5) * mm, "end": v(61.65, 127.5) * mm, "construction": true});
            skLineSegment(sketch, "E81", {"start": v(48.55, 138.5) * mm, "end": v(64.62, 110.66) * mm, "construction": true});
            skLineSegment(sketch, "E82", {"start": v(64.62, 110.66) * mm, "end": v(40, 90) * mm, "construction": true});
            skLineSegment(sketch, "E83", {"start": v(40, 90) * mm, "end": v(15.38, 110.66) * mm, "construction": true});
            skLineSegment(sketch, "E84", {"start": v(15.38, 110.66) * mm, "end": v(31.45, 138.5) * mm, "construction": true});
            skLineSegment(sketch, "E85", {"start": v(61.65, 127.5) * mm, "end": v(56.07, 95.85) * mm, "construction": true});
            skLineSegment(sketch, "E86", {"start": v(56.07, 95.85) * mm, "end": v(23.93, 95.85) * mm, "construction": true});
            skLineSegment(sketch, "E87", {"start": v(23.93, 95.85) * mm, "end": v(18.35, 127.5) * mm, "construction": true});
            skLineSegment(sketch, "E88", {"start": v(18.35, 127.5) * mm, "end": v(48.55, 138.5) * mm, "construction": true});
            skLineSegment(sketch, "E89", {"start": v(31.45, 138.5) * mm, "end": v(48.55, 138.5) * mm});
            skLineSegment(sketch, "E90", {"start": v(48.55, 138.5) * mm, "end": v(61.65, 127.5) * mm});
            skLineSegment(sketch, "E91", {"start": v(61.65, 127.5) * mm, "end": v(64.62, 110.66) * mm});
            skLineSegment(sketch, "E92", {"start": v(64.62, 110.66) * mm, "end": v(56.07, 95.85) * mm});
            skLineSegment(sketch, "E93", {"start": v(56.07, 95.85) * mm, "end": v(40, 90) * mm});
            skLineSegment(sketch, "E94", {"start": v(40, 90) * mm, "end": v(23.93, 95.85) * mm});
            skLineSegment(sketch, "E95", {"start": v(23.93, 95.85) * mm, "end": v(15.38, 110.66) * mm});
            skLineSegment(sketch, "E96", {"start": v(15.38, 110.66) * mm, "end": v(18.35, 127.5) * mm});
            skLineSegment(sketch, "E97", {"start": v(18.35, 127.5) * mm, "end": v(31.45, 138.5) * mm});
            skLineSegment(sketch, "E98.0", {"start": v(17.48, 111.03) * mm, "end": v(20.2, 126.44) * mm});
            skLineSegment(sketch, "E98.1", {"start": v(25.3, 97.48) * mm, "end": v(17.48, 111.03) * mm});
            skLineSegment(sketch, "E98.2", {"start": v(20.2, 126.44) * mm, "end": v(32.18, 136.5) * mm});
            skLineSegment(sketch, "E98.3", {"start": v(40, 92.13) * mm, "end": v(25.3, 97.48) * mm});
            skLineSegment(sketch, "E98.4", {"start": v(54.7, 97.48) * mm, "end": v(40, 92.13) * mm});
            skLineSegment(sketch, "E98.5", {"start": v(32.18, 136.5) * mm, "end": v(47.82, 136.5) * mm});
            skLineSegment(sketch, "E98.6", {"start": v(47.82, 136.5) * mm, "end": v(59.8, 126.44) * mm});
            skLineSegment(sketch, "E98.7", {"start": v(59.8, 126.44) * mm, "end": v(62.52, 111.03) * mm});
            skLineSegment(sketch, "E98.8", {"start": v(62.52, 111.03) * mm, "end": v(54.7, 97.48) * mm});
            skLineSegment(sketch, "E99.0", {"start": v(98.84, 128) * mm, "end": v(133, 128) * mm});
            skLineSegment(sketch, "E99.1", {"start": v(133, 79.22) * mm, "end": v(98.84, 128) * mm});
            skLineSegment(sketch, "E99.2", {"start": v(133, 128) * mm, "end": v(133, 79.22) * mm});
            skSolve(sketch);
        }
        {
            var Q0;
            Q0=makeQuery(id+"F15.imprint","IMPRINT",FACE,{"disambiguationData":[TD([[makeQuery(id+"F15.imprint","IMPRINT",EDGE,{"derivedFrom":sQuery(id+"F15.wireOp",EDGE,"E89")}),-1.0]])]});
            var Q1;
            Q1=makeQuery(id+"F15.imprint","IMPRINT",FACE,{"disambiguationData":[TD([[makeQuery(id+"F15.imprint","IMPRINT",EDGE,{"derivedFrom":sQuery(id+"F15.wireOp",EDGE,"E98.0")}),-1.0]])]});
            var Q2;
            Q2=makeQuery(id+"F15.imprint","IMPRINT",FACE,{"disambiguationData":[TD([[makeQuery(id+"F15.imprint","IMPRINT",EDGE,{"derivedFrom":sQuery(id+"F15.wireOp",EDGE,"E77")}),-1.0]])]});
            var Q3;
            Q3=makeQuery(id+"F15.imprint","IMPRINT",FACE,{"disambiguationData":[TD([[makeQuery(id+"F15.imprint","IMPRINT",EDGE,{"derivedFrom":sQuery(id+"F15.wireOp",EDGE,"E60")}),-1.0]])]});
            var Q4;
            Q4=makeQuery(id+"F15.imprint","IMPRINT",FACE,{"disambiguationData":[TD([[makeQuery(id+"F15.imprint","IMPRINT",EDGE,{"derivedFrom":sQuery(id+"F15.wireOp",EDGE,"E75.0")}),-1.0]])]});
            var Q5;
            Q5=makeQuery(id+"F15.imprint","IMPRINT",FACE,{"disambiguationData":[TD([[makeQuery(id+"F15.imprint","IMPRINT",EDGE,{"derivedFrom":sQuery(id+"F15.wireOp",EDGE,"E99.0")}),-1.0]])]});
            extrude(context, id + "F16", {"entities" : qUnion([Q0, Q1, Q2, Q3, Q4, Q5]), "operationType" : NewBodyOperationType.REMOVE, "oppositeDirection" : true, "depth" : 25 * mm, "offsetDistance" : 25 * mm});
        }
        {
            var Q0;
            Q0=makeQuery(id+"F15.imprint","IMPRINT",FACE,{"disambiguationData":[TD([[makeQuery(id+"F15.imprint","IMPRINT",EDGE,{"derivedFrom":sQuery(id+"F15.wireOp",EDGE,"E98.0")}),-1.0]])]});
            var Q1;
            Q1=makeQuery(id+"F15.imprint","IMPRINT",FACE,{"disambiguationData":[TD([[makeQuery(id+"F15.imprint","IMPRINT",EDGE,{"derivedFrom":sQuery(id+"F15.wireOp",EDGE,"E99.0")}),-1.0]])]});
            var Q2;
            Q2=makeQuery(id+"F15.imprint","IMPRINT",FACE,{"disambiguationData":[TD([[makeQuery(id+"F15.imprint","IMPRINT",EDGE,{"derivedFrom":sQuery(id+"F15.wireOp",EDGE,"E75.0")}),-1.0]])]});
            extrude(context, id + "F17", {"entities" : qUnion([Q0, Q1, Q2]), "depth" : 30 * mm, "offsetDistance" : 25 * mm});
        }
        {
            var Q0;
            Q0=makeQuery(id+"F1.opExtrude","SWEPT_FACE",FACE,{"disambiguationData":[OSD([sQuery(id+"F0.wireOp",EDGE,"E0.left")])]});
            var sketch = newSketch(context, id + "F18", { "sketchPlane" : qUnion([Q0])});
            skCircle(sketch, "E100.cCircle", {"center": v(40, 110) * mm, "radius": 30 * mm, "construction": true});
            skLineSegment(sketch, "E100.0", {"start": v(65.98, 125) * mm, "end": v(69.54, 104.8) * mm, "construction": true});
            skLineSegment(sketch, "E100.1", {"start": v(69.54, 104.8) * mm, "end": v(59.28, 87.02) * mm, "construction": true});
            skLineSegment(sketch, "E100.2", {"start": v(59.28, 87.02) * mm, "end": v(40, 80) * mm, "construction": true});
            skLineSegment(sketch, "E100.3", {"start": v(40, 80) * mm, "end": v(20.72, 87.02) * mm, "construction": true});
            skLineSegment(sketch, "E100.4", {"start": v(20.72, 87.02) * mm, "end": v(10.46, 104.8) * mm, "construction": true});
            skLineSegment(sketch, "E100.5", {"start": v(10.46, 104.8) * mm, "end": v(14.02, 125) * mm, "construction": true});
            skLineSegment(sketch, "E100.6", {"start": v(14.02, 125) * mm, "end": v(29.74, 138.2) * mm, "construction": true});
            skLineSegment(sketch, "E100.7", {"start": v(29.74, 138.2) * mm, "end": v(50.26, 138.2) * mm, "construction": true});
            skLineSegment(sketch, "E100.8", {"start": v(50.26, 138.2) * mm, "end": v(65.98, 125) * mm, "construction": true});
            skLineSegment(sketch, "E101", {"start": v(50.26, 138.2) * mm, "end": v(52.59, 125) * mm, "construction": true});
            skLineSegment(sketch, "E102", {"start": v(65.98, 125) * mm, "end": v(59.28, 113.4) * mm, "construction": true});
            skLineSegment(sketch, "E103", {"start": v(69.54, 104.8) * mm, "end": v(56.96, 100.2) * mm, "construction": true});
            skLineSegment(sketch, "E104", {"start": v(59.28, 87.02) * mm, "end": v(46.7, 91.6) * mm, "construction": true});
            skLineSegment(sketch, "E105", {"start": v(40, 80) * mm, "end": v(33.3, 91.6) * mm, "construction": true});
            skLineSegment(sketch, "E106", {"start": v(20.72, 87.02) * mm, "end": v(23.04, 100.2) * mm, "construction": true});
            skLineSegment(sketch, "E107", {"start": v(10.46, 104.8) * mm, "end": v(20.72, 113.4) * mm, "construction": true});
            skLineSegment(sketch, "E108", {"start": v(14.02, 125) * mm, "end": v(27.41, 125) * mm, "construction": true});
            skLineSegment(sketch, "E109", {"start": v(29.74, 138.2) * mm, "end": v(40, 129.58) * mm, "construction": true});
            skLineSegment(sketch, "E110", {"start": v(29.74, 138.2) * mm, "end": v(40, 129.58) * mm});
            skLineSegment(sketch, "E111", {"start": v(40, 129.58) * mm, "end": v(50.26, 138.2) * mm});
            skLineSegment(sketch, "E112", {"start": v(50.26, 138.2) * mm, "end": v(52.59, 125) * mm});
            skLineSegment(sketch, "E113", {"start": v(52.59, 125) * mm, "end": v(65.98, 125) * mm});
            skLineSegment(sketch, "E114", {"start": v(65.98, 125) * mm, "end": v(59.28, 113.4) * mm});
            skLineSegment(sketch, "E115", {"start": v(59.28, 113.4) * mm, "end": v(69.54, 104.8) * mm});
            skLineSegment(sketch, "E116", {"start": v(69.54, 104.8) * mm, "end": v(56.96, 100.2) * mm});
            skLineSegment(sketch, "E117", {"start": v(56.96, 100.2) * mm, "end": v(59.28, 87.02) * mm});
            skLineSegment(sketch, "E118", {"start": v(59.28, 87.02) * mm, "end": v(46.7, 91.6) * mm});
            skLineSegment(sketch, "E119", {"start": v(46.7, 91.6) * mm, "end": v(40, 80) * mm});
            skLineSegment(sketch, "E120", {"start": v(40, 80) * mm, "end": v(33.3, 91.6) * mm});
            skLineSegment(sketch, "E121", {"start": v(33.3, 91.6) * mm, "end": v(20.72, 87.02) * mm});
            skLineSegment(sketch, "E122", {"start": v(20.72, 87.02) * mm, "end": v(23.04, 100.2) * mm});
            skLineSegment(sketch, "E123", {"start": v(23.04, 100.2) * mm, "end": v(10.46, 104.8) * mm});
            skLineSegment(sketch, "E124", {"start": v(10.46, 104.8) * mm, "end": v(20.72, 113.4) * mm});
            skLineSegment(sketch, "E125", {"start": v(20.72, 113.4) * mm, "end": v(14.02, 125) * mm});
            skLineSegment(sketch, "E126", {"start": v(14.02, 125) * mm, "end": v(27.41, 125) * mm});
            skLineSegment(sketch, "E127", {"start": v(27.41, 125) * mm, "end": v(29.74, 138.2) * mm});
            skLineSegment(sketch, "E128", {"start": v(40, 129.58) * mm, "end": v(40, 80) * mm, "construction": true});
            skLineSegment(sketch, "E129.trimOffspring", {"start": v(45.46, 125) * mm, "end": v(53.82, 117.98) * mm, "construction": true});
            skLineSegment(sketch, "E130.trimOffspring", {"start": v(40, 129.58) * mm, "end": v(50.26, 138.2) * mm, "construction": true});
            skLineSegment(sketch, "E131.trimOffspring", {"start": v(34.54, 125) * mm, "end": v(45.46, 125) * mm, "construction": true});
            skLineSegment(sketch, "E132.trimOffspring", {"start": v(52.59, 125) * mm, "end": v(65.98, 125) * mm, "construction": true});
            skLineSegment(sketch, "E133.trimOffspring", {"start": v(53.82, 117.98) * mm, "end": v(55.72, 107.23) * mm, "construction": true});
            skLineSegment(sketch, "E134.trimOffspring", {"start": v(59.28, 113.4) * mm, "end": v(69.54, 104.8) * mm, "construction": true});
            skLineSegment(sketch, "E135.trimOffspring", {"start": v(55.72, 107.23) * mm, "end": v(50.26, 97.77) * mm, "construction": true});
            skLineSegment(sketch, "E136.trimOffspring", {"start": v(56.96, 100.2) * mm, "end": v(59.28, 87.02) * mm, "construction": true});
            skLineSegment(sketch, "E137.trimOffspring", {"start": v(50.26, 97.77) * mm, "end": v(40, 94.04) * mm, "construction": true});
            skLineSegment(sketch, "E138.trimOffspring", {"start": v(46.7, 91.6) * mm, "end": v(40, 80) * mm, "construction": true});
            skLineSegment(sketch, "E139.trimOffspring", {"start": v(40, 94.04) * mm, "end": v(29.74, 97.77) * mm, "construction": true});
            skLineSegment(sketch, "E140.trimOffspring", {"start": v(33.3, 91.6) * mm, "end": v(20.72, 87.02) * mm, "construction": true});
            skLineSegment(sketch, "E141.trimOffspring", {"start": v(23.04, 100.2) * mm, "end": v(10.46, 104.8) * mm, "construction": true});
            skLineSegment(sketch, "E142.trimOffspring", {"start": v(29.74, 97.77) * mm, "end": v(24.28, 107.23) * mm, "construction": true});
            skLineSegment(sketch, "E143.trimOffspring", {"start": v(24.28, 107.23) * mm, "end": v(26.18, 117.98) * mm, "construction": true});
            skLineSegment(sketch, "E144.trimOffspring", {"start": v(20.72, 113.4) * mm, "end": v(14.02, 125) * mm, "construction": true});
            skLineSegment(sketch, "E145.trimOffspring", {"start": v(26.18, 117.98) * mm, "end": v(34.54, 125) * mm, "construction": true});
            skLineSegment(sketch, "E146.trimOffspring", {"start": v(27.41, 125) * mm, "end": v(29.74, 138.2) * mm, "construction": true});
            skLineSegment(sketch, "E147.0", {"start": v(29.1, 123) * mm, "end": v(31.1, 134.43) * mm});
            skLineSegment(sketch, "E147.1", {"start": v(17.48, 123) * mm, "end": v(29.1, 123) * mm});
            skLineSegment(sketch, "E147.2", {"start": v(23.29, 112.95) * mm, "end": v(17.48, 123) * mm});
            skLineSegment(sketch, "E147.3", {"start": v(14.4, 105.49) * mm, "end": v(23.29, 112.95) * mm});
            skLineSegment(sketch, "E147.4", {"start": v(25.3, 101.51) * mm, "end": v(14.4, 105.49) * mm});
            skLineSegment(sketch, "E147.5", {"start": v(31.1, 134.43) * mm, "end": v(40, 126.97) * mm});
            skLineSegment(sketch, "E147.6", {"start": v(23.29, 90.08) * mm, "end": v(25.3, 101.51) * mm});
            skLineSegment(sketch, "E147.7", {"start": v(34.2, 94.05) * mm, "end": v(23.29, 90.08) * mm});
            skLineSegment(sketch, "E147.8", {"start": v(62.52, 123) * mm, "end": v(56.71, 112.95) * mm});
            skLineSegment(sketch, "E147.9", {"start": v(50.9, 123) * mm, "end": v(62.52, 123) * mm});
            skLineSegment(sketch, "E147.10", {"start": v(48.9, 134.43) * mm, "end": v(50.9, 123) * mm});
            skLineSegment(sketch, "E147.11", {"start": v(40, 126.97) * mm, "end": v(48.9, 134.43) * mm});
            skLineSegment(sketch, "E147.12", {"start": v(56.71, 112.95) * mm, "end": v(65.6, 105.49) * mm});
            skLineSegment(sketch, "E147.13", {"start": v(65.6, 105.49) * mm, "end": v(54.7, 101.51) * mm});
            skLineSegment(sketch, "E147.14", {"start": v(54.7, 101.51) * mm, "end": v(56.71, 90.08) * mm});
            skLineSegment(sketch, "E147.15", {"start": v(56.71, 90.08) * mm, "end": v(45.8, 94.05) * mm});
            skLineSegment(sketch, "E147.16", {"start": v(45.8, 94.05) * mm, "end": v(40, 84) * mm});
            skLineSegment(sketch, "E147.17", {"start": v(40, 84) * mm, "end": v(34.2, 94.05) * mm});
            skLineSegment(sketch, "E148.0", {"start": v(-5, -5) * mm, "end": v(155, -5) * mm});
            skLineSegment(sketch, "E148.1", {"start": v(-5, 155) * mm, "end": v(-5, -5) * mm});
            skLineSegment(sketch, "E148.2", {"start": v(155, 155) * mm, "end": v(-5, 155) * mm});
            skLineSegment(sketch, "E148.3", {"start": v(155, -5) * mm, "end": v(155, 155) * mm});
            skLineSegment(sketch, "E149.bottom", {"start": v(30.44, 10) * mm, "end": v(107.5, 10) * mm});
            skLineSegment(sketch, "E149.top", {"start": v(42.5, 55) * mm, "end": v(119.56, 55) * mm});
            skLineSegment(sketch, "E149.left", {"start": v(30.44, 10) * mm, "end": v(42.5, 55) * mm});
            skLineSegment(sketch, "E149.right", {"start": v(107.5, 10) * mm, "end": v(119.56, 55) * mm});
            skLineSegment(sketch, "E150", {"start": v(113.53, 32.5) * mm, "end": v(36.47, 32.5) * mm, "construction": true});
            skLineSegment(sketch, "E151", {"start": v(75, 0) * mm, "end": v(75, 32.5) * mm, "construction": true});
            skLineSegment(sketch, "E152.0", {"start": v(44.03, 53) * mm, "end": v(116.95, 53) * mm});
            skLineSegment(sketch, "E152.1", {"start": v(33.05, 12) * mm, "end": v(44.03, 53) * mm});
            skLineSegment(sketch, "E152.2", {"start": v(33.05, 12) * mm, "end": v(105.97, 12) * mm});
            skLineSegment(sketch, "E152.3", {"start": v(105.97, 12) * mm, "end": v(116.95, 53) * mm});
            skLineSegment(sketch, "E153", {"start": v(90, 140) * mm, "end": v(115, 79.64) * mm});
            skLineSegment(sketch, "E154", {"start": v(115, 79.64) * mm, "end": v(140, 140) * mm});
            skLineSegment(sketch, "E155", {"start": v(140, 140) * mm, "end": v(126.07, 140) * mm});
            skLineSegment(sketch, "E156", {"start": v(126.07, 140) * mm, "end": v(115, 113.28) * mm});
            skLineSegment(sketch, "E157", {"start": v(115, 113.28) * mm, "end": v(103.93, 140) * mm});
            skLineSegment(sketch, "E158", {"start": v(103.93, 140) * mm, "end": v(90, 140) * mm});
            skLineSegment(sketch, "E159.0", {"start": v(127.4, 138) * mm, "end": v(115, 108.05) * mm});
            skLineSegment(sketch, "E159.1", {"start": v(102.6, 138) * mm, "end": v(93, 138) * mm});
            skLineSegment(sketch, "E159.2", {"start": v(93, 138) * mm, "end": v(115, 84.87) * mm});
            skLineSegment(sketch, "E159.3", {"start": v(115, 108.05) * mm, "end": v(102.6, 138) * mm});
            skLineSegment(sketch, "E159.4", {"start": v(115, 84.87) * mm, "end": v(137, 138) * mm});
            skLineSegment(sketch, "E159.5", {"start": v(137, 138) * mm, "end": v(127.4, 138) * mm});
            skSolve(sketch);
        }
        {
            var Q0;
            Q0=makeQuery(id+"F18.imprint","IMPRINT",FACE,{"disambiguationData":[TD([[makeQuery(id+"F18.imprint","IMPRINT",EDGE,{"derivedFrom":sQuery(id+"F18.wireOp",EDGE,"E110")}),-1.0]])]});
            var Q1;
            Q1=makeQuery(id+"F18.imprint","IMPRINT",FACE,{"disambiguationData":[TD([[makeQuery(id+"F18.imprint","IMPRINT",EDGE,{"derivedFrom":sQuery(id+"F18.wireOp",EDGE,"E147.0")}),-1.0]])]});
            var Q2;
            Q2=makeQuery(id+"F18.imprint","IMPRINT",FACE,{"disambiguationData":[TD([[makeQuery(id+"F18.imprint","IMPRINT",EDGE,{"derivedFrom":sQuery(id+"F18.wireOp",EDGE,"E153")}),1.0]])]});
            var Q3;
            Q3=makeQuery(id+"F18.imprint","IMPRINT",FACE,{"disambiguationData":[TD([[makeQuery(id+"F18.imprint","IMPRINT",EDGE,{"derivedFrom":sQuery(id+"F18.wireOp",EDGE,"E159.0")}),1.0]])]});
            var Q4;
            Q4=makeQuery(id+"F18.imprint","IMPRINT",FACE,{"disambiguationData":[TD([[makeQuery(id+"F18.imprint","IMPRINT",EDGE,{"derivedFrom":sQuery(id+"F18.wireOp",EDGE,"E149.bottom")}),1.0]])]});
            var Q5;
            Q5=makeQuery(id+"F18.imprint","IMPRINT",FACE,{"disambiguationData":[TD([[makeQuery(id+"F18.imprint","IMPRINT",EDGE,{"derivedFrom":sQuery(id+"F18.wireOp",EDGE,"E152.0")}),-1.0]])]});
            extrude(context, id + "F19", {"entities" : qUnion([Q0, Q1, Q2, Q3, Q4, Q5]), "operationType" : NewBodyOperationType.REMOVE, "oppositeDirection" : true, "depth" : 25 * mm, "offsetDistance" : 25 * mm});
        }
        {
            var Q0;
            Q0=makeQuery(id+"F18.imprint","IMPRINT",FACE,{"disambiguationData":[TD([[makeQuery(id+"F18.imprint","IMPRINT",EDGE,{"derivedFrom":sQuery(id+"F18.wireOp",EDGE,"E147.0")}),-1.0]])]});
            var Q1;
            Q1=makeQuery(id+"F18.imprint","IMPRINT",FACE,{"disambiguationData":[TD([[makeQuery(id+"F18.imprint","IMPRINT",EDGE,{"derivedFrom":sQuery(id+"F18.wireOp",EDGE,"E159.0")}),1.0]])]});
            var Q2;
            Q2=makeQuery(id+"F18.imprint","IMPRINT",FACE,{"disambiguationData":[TD([[makeQuery(id+"F18.imprint","IMPRINT",EDGE,{"derivedFrom":sQuery(id+"F18.wireOp",EDGE,"E152.0")}),-1.0]])]});
            extrude(context, id + "F20", {"entities" : qUnion([Q0, Q1, Q2]), "depth" : 30 * mm, "offsetDistance" : 25 * mm});
        }
    });
